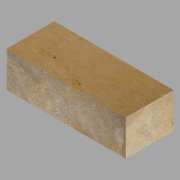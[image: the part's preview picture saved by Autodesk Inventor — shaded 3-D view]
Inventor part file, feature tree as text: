
AUTODESK INVENTOR PART (.ipt)
format: ipt  version: 2022.2 (Build 262287000, 287)  size: 134,656 bytes
history: native  units: in
note: dims shown in document units (in); Inventor stores cm internally (conversion verified against a paired STEP export)
features: extrude x1, sketch x1
ambient origin geometry x8: Origin, YZ Plane, XZ Plane, XY Plane, X Axis, Y Axis, Z Axis, Center Point
bodies: Solid1 (feature_tree)
feature tree (2):
  extrude  "Extrusion1"  Depth=24.0in
  sketch  "Sketch1"  dims[d0=18.0in d1=24.0in d2=60.0in d3=0.0in]
